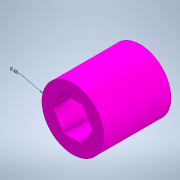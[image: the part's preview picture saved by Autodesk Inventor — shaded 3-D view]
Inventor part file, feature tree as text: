
AUTODESK INVENTOR PART (.ipt)
format: ipt  version: 2022.1 (Build 261234000, 234)  size: 122,880 bytes
history: native  units: in
note: dims shown in document units (in); Inventor stores cm internally (conversion verified against a paired STEP export)
features: other x3, extrude x1, sketch x1
ambient origin geometry x8: Origin, YZ Plane, XZ Plane, XY Plane, X Axis, Y Axis, Z Axis, Center Point
bodies: Solid1 (feature_tree)
feature tree (5):
  other  "Annotations"
  extrude  "Extrusion1"  Depth=0.75in
  other  "Thicken Hex"
  sketch  "Sketch1"  dims[d0=0.375in d2=0.6875in d3=0.1272in d4=0.75in d5=0.0in d6=0.005in d7=0.005in d8=1.1428in d9=0.6875in]
  other  "Diameter Dimension 1"
